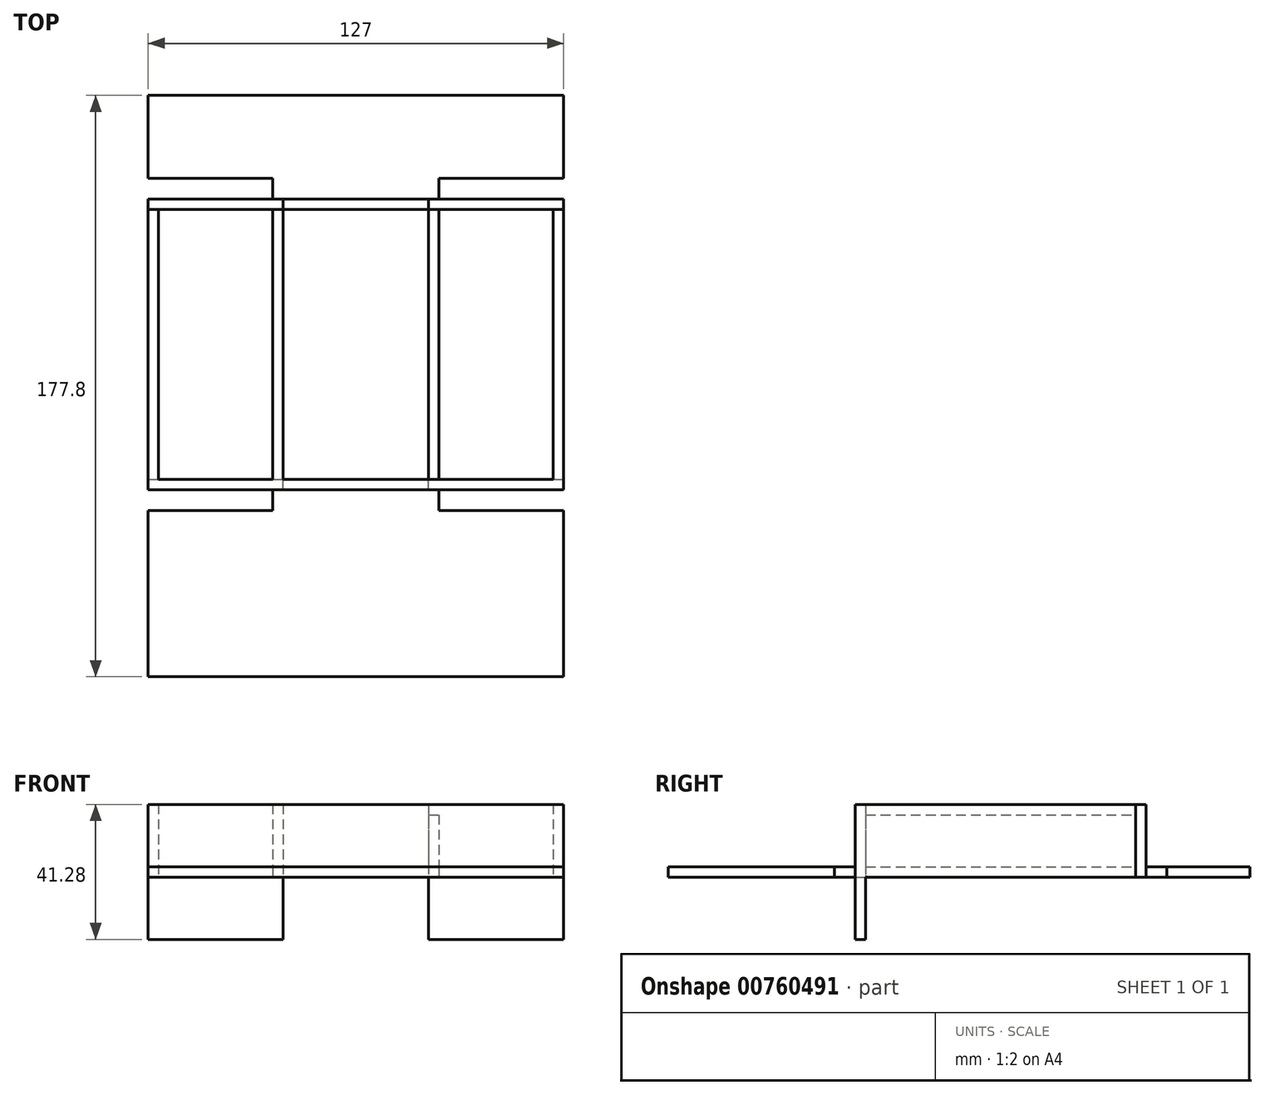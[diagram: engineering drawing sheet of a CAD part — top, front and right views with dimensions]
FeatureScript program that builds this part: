
annotation { "Feature Type Name" : "Feature", "Feature Type Description" : "" }
export const myFeature = defineFeature(function(context is Context, id is Id, definition is map)
    precondition{}
    {
        {
            var Q0;
            Q0=qCreatedBy(makeId("Top.planeOp"),FACE);
            var sketch = newSketch(context, id + "F0", { "sketchPlane" : qUnion([Q0])});
            skLineSegment(sketch, "E0.bottom", {"start": v(0, 0) * mm, "end": v(127, 0) * mm});
            skLineSegment(sketch, "E0.top", {"start": v(0, 177.8) * mm, "end": v(127, 177.8) * mm});
            skLineSegment(sketch, "E0.left", {"start": v(0, 0) * mm, "end": v(0, 177.8) * mm});
            skLineSegment(sketch, "E0.right", {"start": v(127, 0) * mm, "end": v(127, 177.8) * mm});
            skLineSegment(sketch, "E1.top", {"start": v(0, 57.15) * mm, "end": v(127, 57.15) * mm});
            skLineSegment(sketch, "E1.left", {"start": v(0, 0) * mm, "end": v(0, 57.15) * mm});
            skLineSegment(sketch, "E1.right", {"start": v(127, 0) * mm, "end": v(127, 57.15) * mm});
            skLineSegment(sketch, "E2.top", {"start": v(0, 146.05) * mm, "end": v(127, 146.05) * mm});
            skLineSegment(sketch, "E2.left", {"start": v(0, 177.8) * mm, "end": v(0, 146.05) * mm});
            skLineSegment(sketch, "E2.right", {"start": v(127, 177.8) * mm, "end": v(127, 146.05) * mm});
            skLineSegment(sketch, "E3.bottom", {"start": v(0, 146.05) * mm, "end": v(3.17, 146.05) * mm});
            skLineSegment(sketch, "E3.top", {"start": v(0, 57.15) * mm, "end": v(3.17, 57.15) * mm});
            skLineSegment(sketch, "E3.left", {"start": v(0, 146.05) * mm, "end": v(0, 57.15) * mm});
            skLineSegment(sketch, "E3.right", {"start": v(3.17, 146.05) * mm, "end": v(3.17, 57.15) * mm});
            skLineSegment(sketch, "E4.bottom", {"start": v(127, 146.05) * mm, "end": v(123.82, 146.05) * mm});
            skLineSegment(sketch, "E4.top", {"start": v(127, 57.15) * mm, "end": v(123.82, 57.15) * mm});
            skLineSegment(sketch, "E4.left", {"start": v(127, 146.05) * mm, "end": v(127, 57.15) * mm});
            skLineSegment(sketch, "E4.right", {"start": v(123.82, 146.05) * mm, "end": v(123.82, 57.15) * mm});
            skLineSegment(sketch, "E5.top", {"start": v(0, 142.88) * mm, "end": v(127, 142.88) * mm});
            skLineSegment(sketch, "E5.left", {"start": v(0, 146.05) * mm, "end": v(0, 142.88) * mm});
            skLineSegment(sketch, "E5.right", {"start": v(127, 146.05) * mm, "end": v(127, 142.88) * mm});
            skLineSegment(sketch, "E6.top", {"start": v(0, 60.33) * mm, "end": v(127, 60.33) * mm});
            skLineSegment(sketch, "E6.left", {"start": v(0, 57.15) * mm, "end": v(0, 60.33) * mm});
            skLineSegment(sketch, "E6.right", {"start": v(127, 57.15) * mm, "end": v(127, 60.33) * mm});
            skLineSegment(sketch, "E7", {"start": v(0, 57.15) * mm, "end": v(38.1, 57.15) * mm});
            skLineSegment(sketch, "E8.bottom", {"start": v(38.1, 57.15) * mm, "end": v(41.27, 57.15) * mm});
            skLineSegment(sketch, "E8.top", {"start": v(38.1, 146.05) * mm, "end": v(41.27, 146.05) * mm});
            skLineSegment(sketch, "E8.left", {"start": v(38.1, 57.15) * mm, "end": v(38.1, 146.05) * mm});
            skLineSegment(sketch, "E8.right", {"start": v(41.27, 57.15) * mm, "end": v(41.27, 146.05) * mm});
            skLineSegment(sketch, "E9", {"start": v(127, 57.15) * mm, "end": v(88.9, 57.15) * mm});
            skLineSegment(sketch, "E10.bottom", {"start": v(88.9, 57.15) * mm, "end": v(85.73, 57.15) * mm});
            skLineSegment(sketch, "E10.top", {"start": v(88.9, 146.05) * mm, "end": v(85.72, 146.05) * mm});
            skLineSegment(sketch, "E10.left", {"start": v(88.9, 57.15) * mm, "end": v(88.9, 146.05) * mm});
            skLineSegment(sketch, "E10.right", {"start": v(85.73, 57.15) * mm, "end": v(85.72, 146.05) * mm});
            skLineSegment(sketch, "E11", {"start": v(41.27, 57.15) * mm, "end": v(85.73, 57.15) * mm});
            skLineSegment(sketch, "E12.bottom", {"start": v(38.1, 57.15) * mm, "end": v(0, 57.15) * mm});
            skLineSegment(sketch, "E12.top", {"start": v(38.1, 50.8) * mm, "end": v(0, 50.8) * mm});
            skLineSegment(sketch, "E12.left", {"start": v(38.1, 57.15) * mm, "end": v(38.1, 50.8) * mm});
            skLineSegment(sketch, "E12.right", {"start": v(0, 57.15) * mm, "end": v(0, 50.8) * mm});
            skLineSegment(sketch, "E13.top", {"start": v(127, 50.8) * mm, "end": v(88.9, 50.8) * mm});
            skLineSegment(sketch, "E13.left", {"start": v(127, 57.15) * mm, "end": v(127, 50.8) * mm});
            skLineSegment(sketch, "E13.right", {"start": v(88.9, 57.15) * mm, "end": v(88.9, 50.8) * mm});
            skLineSegment(sketch, "E14.bottom", {"start": v(127, 146.05) * mm, "end": v(88.9, 146.05) * mm});
            skLineSegment(sketch, "E14.top", {"start": v(127, 152.4) * mm, "end": v(88.9, 152.4) * mm});
            skLineSegment(sketch, "E14.left", {"start": v(127, 146.05) * mm, "end": v(127, 152.4) * mm});
            skLineSegment(sketch, "E14.right", {"start": v(88.9, 146.05) * mm, "end": v(88.9, 152.4) * mm});
            skLineSegment(sketch, "E15.bottom", {"start": v(0, 146.05) * mm, "end": v(38.1, 146.05) * mm});
            skLineSegment(sketch, "E15.top", {"start": v(0, 152.4) * mm, "end": v(38.1, 152.4) * mm});
            skLineSegment(sketch, "E15.left", {"start": v(0, 146.05) * mm, "end": v(0, 152.4) * mm});
            skLineSegment(sketch, "E15.right", {"start": v(38.1, 146.05) * mm, "end": v(38.1, 152.4) * mm});
            skSolve(sketch);
        }
        {
            var Q0;
            {var subQ4=sQuery(id+"F0.wireOp",EDGE,"E0.bottom");Q0=makeQuery(id+"F0.imprint","IMPRINT",FACE,{"disambiguationData":[TD([[makeQuery(id+"F0.imprint","IMPRINT",EDGE,{"derivedFrom":subQ4}),1.0]])]});}
            var Q1;
            {var subQ3=sQuery(id+"F0.wireOp",EDGE,"E0.top");Q1=makeQuery(id+"F0.imprint","IMPRINT",FACE,{"disambiguationData":[TD([[makeQuery(id+"F0.imprint","IMPRINT",EDGE,{"derivedFrom":subQ3}),-1.0]])]});}
            var Q2;
            {var subQ0=sQuery(id+"F0.wireOp",EDGE,"E8.right");var subQ1=sQuery(id+"F0.wireOp",EDGE,"E5.top");var subQ2=makeQuery(id+"F0.imprint","INTERSECT",VERTEX,{"derivedFrom":[subQ1,subQ0]});Q2=makeQuery(id+"F0.imprint","IMPRINT",FACE,{"disambiguationData":[TD([[makeQuery(id+"F0.imprint","IMPRINT",EDGE,{"disambiguationData":[TD([[subQ2,-1.0]])],"derivedFrom":subQ1}),-1.0]])]});}
            extrude(context, id + "F1", {"entities" : qUnion([Q0, Q1, Q2]), "depth" : 3.17 * mm, "offsetDistance" : 25.4 * mm});
        }
        {
            var Q0;
            {var subQ0=sQuery(id+"F0.wireOp",EDGE,"E4.right");var subQ1=sQuery(id+"F0.wireOp",EDGE,"E1.top");var subQ2=makeQuery(id+"F0.imprint","INTERSECT",VERTEX,{"derivedFrom":[subQ1,subQ0]});Q0=makeQuery(id+"F0.imprint","IMPRINT",FACE,{"disambiguationData":[TD([[makeQuery(id+"F0.imprint","IMPRINT",EDGE,{"disambiguationData":[TD([[subQ2,1.0]])],"derivedFrom":subQ0}),-1.0]])]});}
            var Q1;
            {var subQ0=sQuery(id+"F0.wireOp",EDGE,"E6.top");var subQ1=sQuery(id+"F0.wireOp",EDGE,"E0.right");var subQ2=makeQuery(id+"F0.imprint","INTERSECT",VERTEX,{"derivedFrom":[subQ1,subQ0]});Q1=makeQuery(id+"F0.imprint","IMPRINT",FACE,{"disambiguationData":[TD([[makeQuery(id+"F0.imprint","IMPRINT",EDGE,{"disambiguationData":[TD([[subQ2,1.0]])],"derivedFrom":subQ1}),1.0]])]});}
            var Q2;
            {var subQ0=sQuery(id+"F0.wireOp",EDGE,"E10.left");var subQ5=sQuery(id+"F0.wireOp",EDGE,"E6.top");var subQ6=makeQuery(id+"F0.imprint","INTERSECT",VERTEX,{"derivedFrom":[subQ5,subQ0]});Q2=makeQuery(id+"F0.imprint","IMPRINT",FACE,{"disambiguationData":[TD([[makeQuery(id+"F0.imprint","IMPRINT",EDGE,{"disambiguationData":[TD([[subQ6,1.0]])],"derivedFrom":subQ5}),-1.0]])]});}
            extrude(context, id + "F2", {"entities" : qUnion([Q0, Q1, Q2]), "depth" : 22.22 * mm, "offsetDistance" : 25.4 * mm});
        }
        {
            var Q0;
            {var subQ0=sQuery(id+"F0.wireOp",EDGE,"E6.top");var subQ1=sQuery(id+"F0.wireOp",EDGE,"E0.right");var subQ2=makeQuery(id+"F0.imprint","INTERSECT",VERTEX,{"derivedFrom":[subQ1,subQ0]});Q0=makeQuery(id+"F0.imprint","IMPRINT",FACE,{"disambiguationData":[TD([[makeQuery(id+"F0.imprint","IMPRINT",EDGE,{"disambiguationData":[TD([[subQ2,-1.0]])],"derivedFrom":subQ1}),1.0]])]});}
            extrude(context, id + "F3", {"entities" : qUnion([Q0]), "depth" : 22.22 * mm, "offsetDistance" : 25.4 * mm});
        }
        {
            var Q0;
            {var subQ0=sQuery(id+"F0.wireOp",EDGE,"E10.right");var subQ1=sQuery(id+"F0.wireOp",EDGE,"E5.top");var subQ2=makeQuery(id+"F0.imprint","INTERSECT",VERTEX,{"derivedFrom":[subQ1,subQ0]});Q0=makeQuery(id+"F0.imprint","IMPRINT",FACE,{"disambiguationData":[TD([[makeQuery(id+"F0.imprint","IMPRINT",EDGE,{"disambiguationData":[TD([[subQ2,-1.0]])],"derivedFrom":subQ1}),-1.0]])]});}
            extrude(context, id + "F4", {"entities" : qUnion([Q0]), "depth" : 19.05 * mm, "offsetDistance" : 25.4 * mm});
        }
        {
            var Q0;
            {var subQ0=sQuery(id+"F0.wireOp",EDGE,"E2.top");var subQ1=sQuery(id+"F0.wireOp",EDGE,"E0.right");var subQ2=makeQuery(id+"F0.imprint","INTERSECT",VERTEX,{"derivedFrom":[subQ1,subQ0]});Q0=makeQuery(id+"F0.imprint","IMPRINT",FACE,{"disambiguationData":[TD([[makeQuery(id+"F0.imprint","IMPRINT",EDGE,{"disambiguationData":[TD([[subQ2,1.0]])],"derivedFrom":subQ1}),1.0]])]});}
            var Q1;
            {var subQ3=sQuery(id+"F0.wireOp",EDGE,"E4.right");var subQ5=sQuery(id+"F0.wireOp",EDGE,"E5.top");var subQ6=makeQuery(id+"F0.imprint","INTERSECT",VERTEX,{"derivedFrom":[subQ3,subQ5]});Q1=makeQuery(id+"F0.imprint","IMPRINT",FACE,{"disambiguationData":[TD([[makeQuery(id+"F0.imprint","IMPRINT",EDGE,{"disambiguationData":[TD([[subQ6,1.0]])],"derivedFrom":subQ3}),-1.0]])]});}
            var Q2;
            {var subQ3=sQuery(id+"F0.wireOp",EDGE,"E10.right");var subQ5=sQuery(id+"F0.wireOp",EDGE,"E5.top");var subQ6=makeQuery(id+"F0.imprint","INTERSECT",VERTEX,{"derivedFrom":[subQ5,subQ3]});Q2=makeQuery(id+"F0.imprint","IMPRINT",FACE,{"disambiguationData":[TD([[makeQuery(id+"F0.imprint","IMPRINT",EDGE,{"disambiguationData":[TD([[subQ6,-1.0]])],"derivedFrom":subQ5}),1.0]])]});}
            extrude(context, id + "F5", {"entities" : qUnion([Q0, Q1, Q2]), "depth" : 22.22 * mm, "offsetDistance" : 25.4 * mm});
        }
        {
            var Q0;
            {var subQ0=sQuery(id+"F0.wireOp",EDGE,"E2.top");var subQ1=sQuery(id+"F0.wireOp",EDGE,"E0.left");var subQ2=makeQuery(id+"F0.imprint","INTERSECT",VERTEX,{"derivedFrom":[subQ1,subQ0]});Q0=makeQuery(id+"F0.imprint","IMPRINT",FACE,{"disambiguationData":[TD([[makeQuery(id+"F0.imprint","IMPRINT",EDGE,{"disambiguationData":[TD([[subQ2,1.0]])],"derivedFrom":subQ1}),-1.0]])]});}
            var Q1;
            {var subQ3=sQuery(id+"F0.wireOp",EDGE,"E3.right");var subQ5=sQuery(id+"F0.wireOp",EDGE,"E5.top");var subQ6=makeQuery(id+"F0.imprint","INTERSECT",VERTEX,{"derivedFrom":[subQ3,subQ5]});Q1=makeQuery(id+"F0.imprint","IMPRINT",FACE,{"disambiguationData":[TD([[makeQuery(id+"F0.imprint","IMPRINT",EDGE,{"disambiguationData":[TD([[subQ6,1.0]])],"derivedFrom":subQ3}),1.0]])]});}
            var Q2;
            {var subQ0=sQuery(id+"F0.wireOp",EDGE,"E8.right");var subQ5=sQuery(id+"F0.wireOp",EDGE,"E5.top");var subQ6=makeQuery(id+"F0.imprint","INTERSECT",VERTEX,{"derivedFrom":[subQ5,subQ0]});Q2=makeQuery(id+"F0.imprint","IMPRINT",FACE,{"disambiguationData":[TD([[makeQuery(id+"F0.imprint","IMPRINT",EDGE,{"disambiguationData":[TD([[subQ6,1.0]])],"derivedFrom":subQ5}),1.0]])]});}
            extrude(context, id + "F6", {"entities" : qUnion([Q0, Q1, Q2]), "depth" : 22.22 * mm, "offsetDistance" : 25.4 * mm});
        }
        {
            var Q0;
            {var subQ0=sQuery(id+"F0.wireOp",EDGE,"E8.right");var subQ1=sQuery(id+"F0.wireOp",EDGE,"E2.top");var subQ2=makeQuery(id+"F0.imprint","INTERSECT",VERTEX,{"derivedFrom":[subQ1,subQ0]});Q0=makeQuery(id+"F0.imprint","IMPRINT",FACE,{"disambiguationData":[TD([[makeQuery(id+"F0.imprint","IMPRINT",EDGE,{"disambiguationData":[TD([[subQ2,-1.0]])],"derivedFrom":subQ1}),-1.0]])]});}
            extrude(context, id + "F7", {"entities" : qUnion([Q0]), "depth" : 22.22 * mm, "offsetDistance" : 25.4 * mm});
        }
        {
            var Q0;
            {var subQ0=sQuery(id+"F0.wireOp",EDGE,"E6.top");var subQ1=sQuery(id+"F0.wireOp",EDGE,"E0.left");var subQ2=makeQuery(id+"F0.imprint","INTERSECT",VERTEX,{"derivedFrom":[subQ1,subQ0]});Q0=makeQuery(id+"F0.imprint","IMPRINT",FACE,{"disambiguationData":[TD([[makeQuery(id+"F0.imprint","IMPRINT",EDGE,{"disambiguationData":[TD([[subQ2,-1.0]])],"derivedFrom":subQ1}),-1.0]])]});}
            extrude(context, id + "F8", {"entities" : qUnion([Q0]), "depth" : 22.22 * mm, "offsetDistance" : 25.4 * mm});
        }
        {
            var Q0;
            {var subQ0=sQuery(id+"F0.wireOp",EDGE,"E8.right");var subQ1=sQuery(id+"F0.wireOp",EDGE,"E5.top");var subQ2=makeQuery(id+"F0.imprint","INTERSECT",VERTEX,{"derivedFrom":[subQ1,subQ0]});Q0=makeQuery(id+"F0.imprint","IMPRINT",FACE,{"disambiguationData":[TD([[makeQuery(id+"F0.imprint","IMPRINT",EDGE,{"disambiguationData":[TD([[subQ2,1.0]])],"derivedFrom":subQ1}),-1.0]])]});}
            extrude(context, id + "F9", {"entities" : qUnion([Q0]), "depth" : 22.22 * mm, "offsetDistance" : 25.4 * mm});
        }
        {
            var Q0;
            {var subQ0=sQuery(id+"F0.wireOp",EDGE,"E6.top");var subQ1=sQuery(id+"F0.wireOp",EDGE,"E0.left");var subQ2=makeQuery(id+"F0.imprint","INTERSECT",VERTEX,{"derivedFrom":[subQ1,subQ0]});Q0=makeQuery(id+"F0.imprint","IMPRINT",FACE,{"disambiguationData":[TD([[makeQuery(id+"F0.imprint","IMPRINT",EDGE,{"disambiguationData":[TD([[subQ2,1.0]])],"derivedFrom":subQ1}),-1.0]])]});}
            var Q1;
            {var subQ0=sQuery(id+"F0.wireOp",EDGE,"E3.right");var subQ1=sQuery(id+"F0.wireOp",EDGE,"E1.top");var subQ2=makeQuery(id+"F0.imprint","INTERSECT",VERTEX,{"derivedFrom":[subQ1,subQ0]});Q1=makeQuery(id+"F0.imprint","IMPRINT",FACE,{"disambiguationData":[TD([[makeQuery(id+"F0.imprint","IMPRINT",EDGE,{"disambiguationData":[TD([[subQ2,1.0]])],"derivedFrom":subQ0}),1.0]])]});}
            var Q2;
            {var subQ0=sQuery(id+"F0.wireOp",EDGE,"E8.right");var subQ5=sQuery(id+"F0.wireOp",EDGE,"E6.top");var subQ6=makeQuery(id+"F0.imprint","INTERSECT",VERTEX,{"derivedFrom":[subQ5,subQ0]});Q2=makeQuery(id+"F0.imprint","IMPRINT",FACE,{"disambiguationData":[TD([[makeQuery(id+"F0.imprint","IMPRINT",EDGE,{"disambiguationData":[TD([[subQ6,1.0]])],"derivedFrom":subQ5}),-1.0]])]});}
            extrude(context, id + "F10", {"entities" : qUnion([Q0, Q1, Q2]), "depth" : 19.05 * mm + 3.17 * mm, "offsetDistance" : 25.4 * mm});
        }
        {
            var Q0;
            {var subQ0=sQuery(id+"F0.wireOp",EDGE,"E8.right");var subQ1=sQuery(id+"F0.wireOp",EDGE,"E1.top");var subQ2=makeQuery(id+"F0.imprint","INTERSECT",VERTEX,{"derivedFrom":[subQ1,subQ0]});Q0=makeQuery(id+"F0.imprint","IMPRINT",FACE,{"disambiguationData":[TD([[makeQuery(id+"F0.imprint","IMPRINT",EDGE,{"disambiguationData":[TD([[subQ2,-1.0]])],"derivedFrom":subQ1}),1.0]])]});}
            extrude(context, id + "F11", {"entities" : qUnion([Q0]), "depth" : 22.22 * mm, "offsetDistance" : 25.4 * mm});
        }
        {
            var Q0;
            Q0=makeQuery(id+"F2.opExtrude","CAP_FACE",FACE,{"disambiguationData":[OSD([sQuery(id+"F0.wireOp",EDGE,"E0.right"),sQuery(id+"F0.wireOp",EDGE,"E1.top"),sQuery(id+"F0.wireOp",EDGE,"E6.top"),sQuery(id+"F0.wireOp",EDGE,"E10.right")])],"isStart":true});
            extrude(context, id + "F12", {"entities" : qUnion([Q0]), "operationType" : NewBodyOperationType.ADD, "depth" : 19.05 * mm, "offsetDistance" : 25.4 * mm});
        }
        {
            var Q0;
            Q0=makeQuery(id+"F10.opExtrude","CAP_FACE",FACE,{"disambiguationData":[OSD([sQuery(id+"F0.wireOp",EDGE,"E0.left"),sQuery(id+"F0.wireOp",EDGE,"E1.top"),sQuery(id+"F0.wireOp",EDGE,"E6.top"),sQuery(id+"F0.wireOp",EDGE,"E8.right")])],"isStart":true});
            extrude(context, id + "F13", {"entities" : qUnion([Q0]), "operationType" : NewBodyOperationType.ADD, "depth" : 19.05 * mm, "offsetDistance" : 25.4 * mm});
        }
    });
